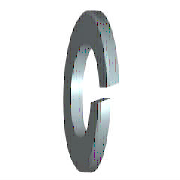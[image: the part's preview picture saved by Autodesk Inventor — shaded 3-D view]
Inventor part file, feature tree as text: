
AUTODESK INVENTOR PART (.ipt)
format: ipt  version: 2025 (Build 290162010, 162A)  size: 126,464 bytes
history: native  units: mm (DEFAULTED — no unit token found)
features: extrude x1, other x1, plane x1
ambient origin geometry x6: Origin, YZ Plane, X Axis, Y Axis, Z Axis, Center Point
bodies: Solid1 (feature_tree), Body (feature_tree)
feature tree (3):
  extrude  "Cut"  Depth=2.6mm
  other  "Work Axis1"
  plane  "Work Plane1"
